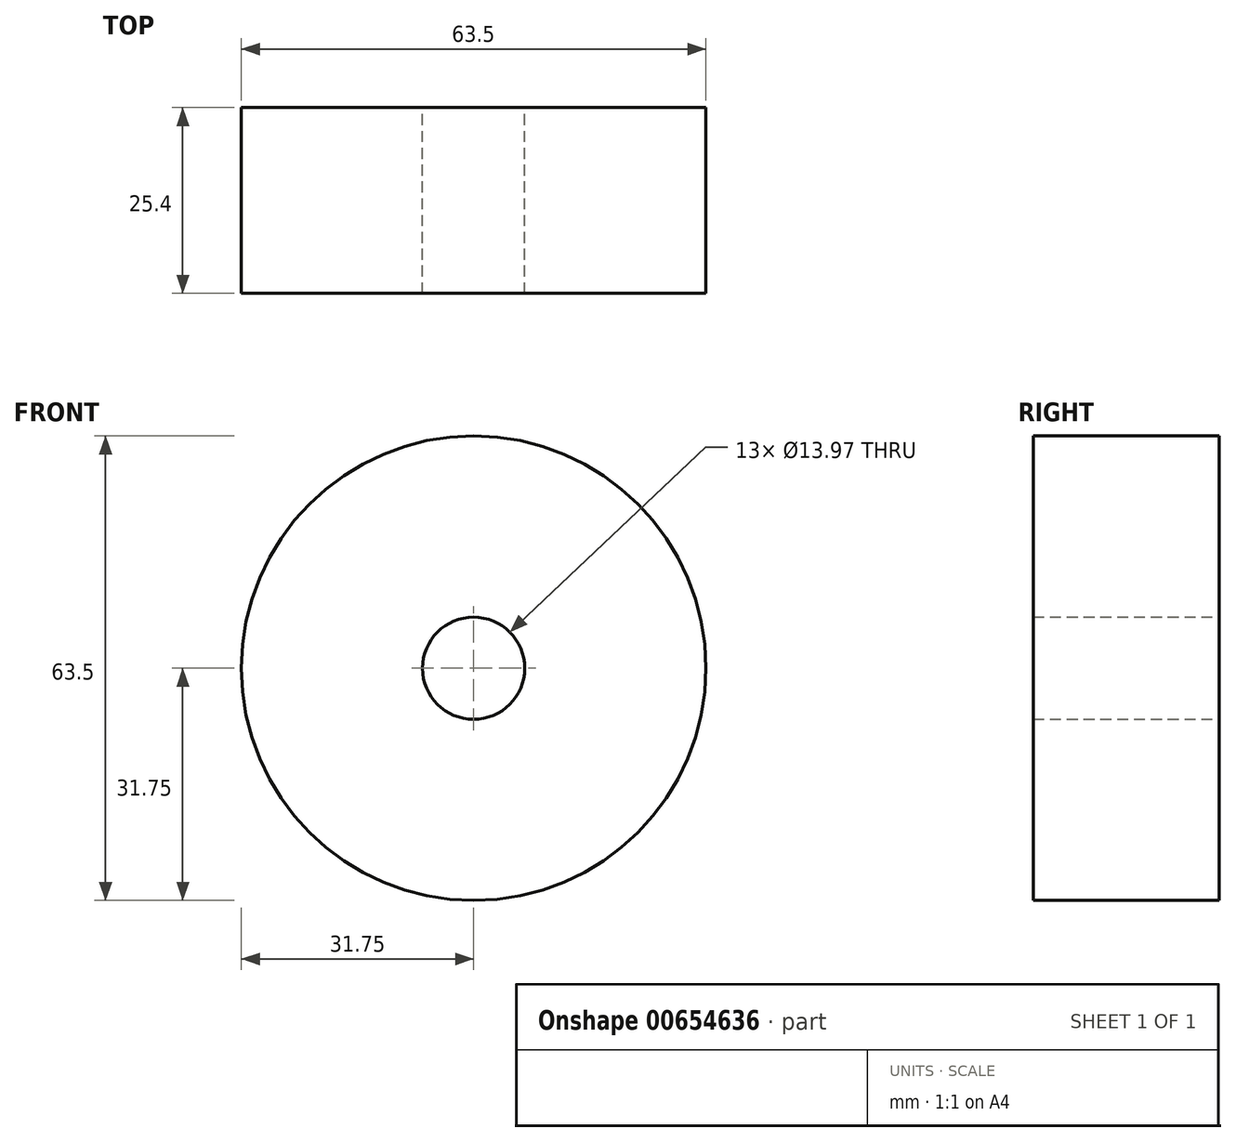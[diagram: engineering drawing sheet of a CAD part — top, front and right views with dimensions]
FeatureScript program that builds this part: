
annotation { "Feature Type Name" : "Feature", "Feature Type Description" : "" }
export const myFeature = defineFeature(function(context is Context, id is Id, definition is map)
    precondition{}
    {
        {
            var Q0;
            Q0=qCreatedBy(makeId("Front.planeOp"),FACE);
            var sketch = newSketch(context, id + "F0", { "sketchPlane" : qUnion([Q0])});
            skCircle(sketch, "E0", {"center": v(0, 0) * mm, "radius": 6.99 * mm});
            skCircle(sketch, "E1", {"center": v(0, 0) * mm, "radius": 31.75 * mm});
            skSolve(sketch);
        }
        {
            var Q0;
            Q0=makeQuery(id+"F0.imprint","IMPRINT",FACE,{"disambiguationData":[TD([[makeQuery(id+"F0.imprint","IMPRINT",EDGE,{"derivedFrom":sQuery(id+"F0.wireOp",EDGE,"E0")}),-1.0]])]});
            var Q1;
            Q1=makeQuery(id+"F0.imprint","IMPRINT",FACE,{"disambiguationData":[TD([[makeQuery(id+"F0.imprint","IMPRINT",EDGE,{"derivedFrom":sQuery(id+"F0.wireOp",EDGE,"Loa4bY2p-woRU-vYDm-CKSG-zThLG4mUhXYQ")}),1.0]])]});
            extrude(context, id + "F1", {"entities" : qUnion([Q0, Q1]), "depth" : 25.4 * mm, "offsetDistance" : 25.4 * mm});
        }
    });
